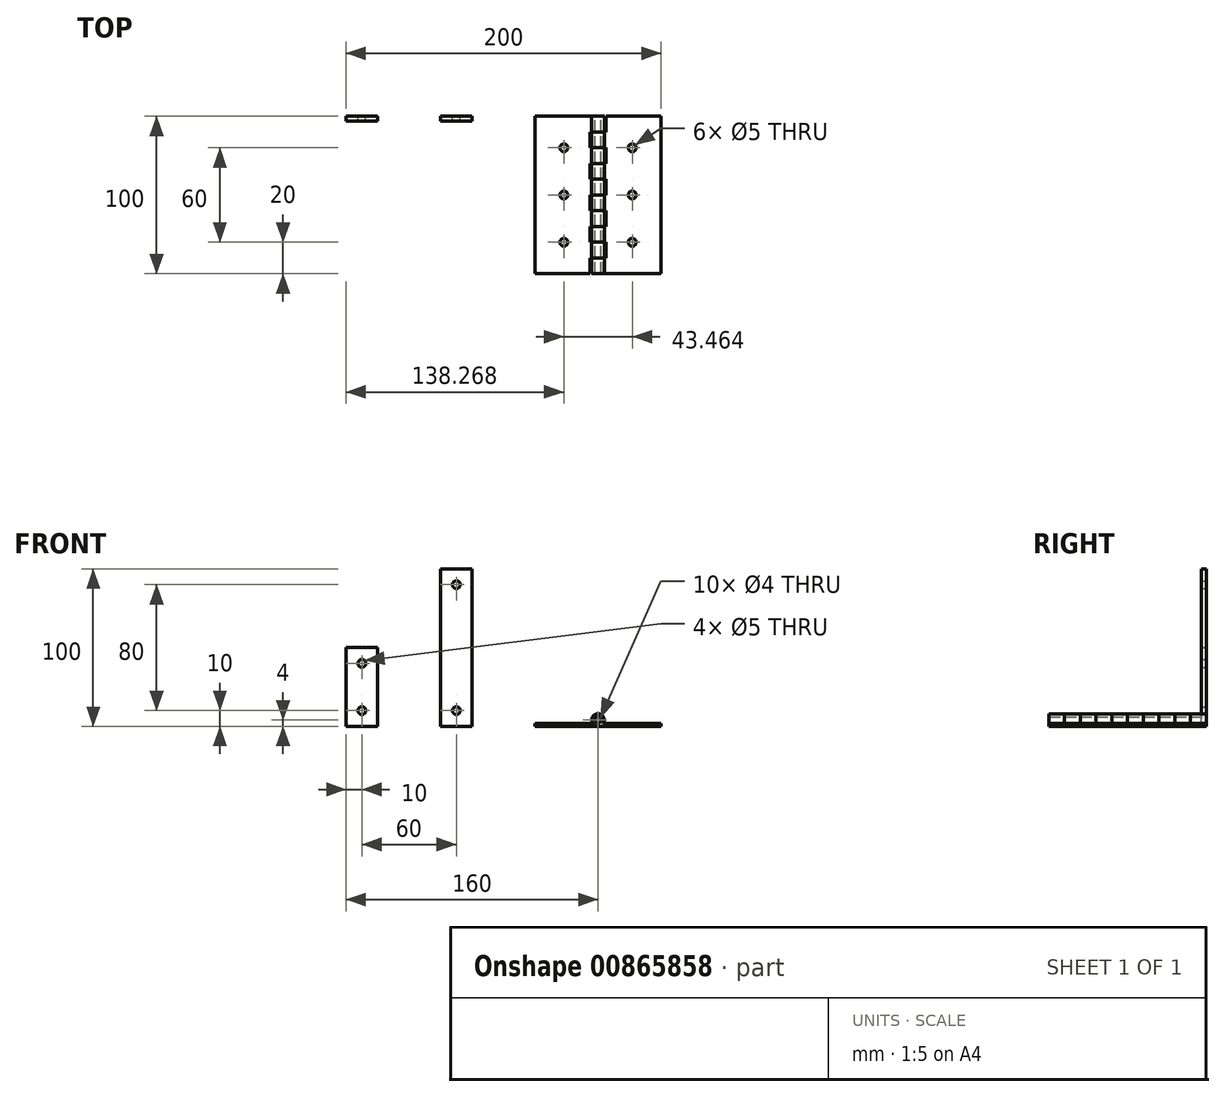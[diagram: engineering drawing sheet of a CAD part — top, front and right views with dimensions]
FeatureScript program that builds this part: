
annotation { "Feature Type Name" : "Feature", "Feature Type Description" : "" }
export const myFeature = defineFeature(function(context is Context, id is Id, definition is map)
    precondition{}
    {
        {
            var Q0;
            Q0=qCreatedBy(makeId("Front.planeOp"),FACE);
            var sketch = newSketch(context, id + "F0", { "sketchPlane" : qUnion([Q0])});
            skLineSegment(sketch, "E0.bottom", {"start": v(-50, 60) * mm, "end": v(-30, 60) * mm});
            skLineSegment(sketch, "E0.top", {"start": v(-50, 10) * mm, "end": v(-30, 10) * mm});
            skLineSegment(sketch, "E0.left", {"start": v(-50, 60) * mm, "end": v(-50, 10) * mm});
            skLineSegment(sketch, "E0.right", {"start": v(-30, 60) * mm, "end": v(-30, 10) * mm});
            skLineSegment(sketch, "E1.bottom", {"start": v(10, 10) * mm, "end": v(30, 10) * mm});
            skLineSegment(sketch, "E1.top", {"start": v(10, 110) * mm, "end": v(30, 110) * mm});
            skLineSegment(sketch, "E1.left", {"start": v(10, 10) * mm, "end": v(10, 110) * mm});
            skLineSegment(sketch, "E1.right", {"start": v(30, 10) * mm, "end": v(30, 110) * mm});
            skLineSegment(sketch, "E2", {"start": v(-40, 10) * mm, "end": v(-40, 60) * mm, "construction": true});
            skCircle(sketch, "E3", {"center": v(-40, 50) * mm, "radius": 2.5 * mm});
            skCircle(sketch, "E4", {"center": v(-40, 20) * mm, "radius": 2.5 * mm});
            skLineSegment(sketch, "E5", {"start": v(20, 10) * mm, "end": v(20, 110) * mm, "construction": true});
            skCircle(sketch, "E6", {"center": v(20, 100) * mm, "radius": 2.5 * mm});
            skCircle(sketch, "E7", {"center": v(20, 20) * mm, "radius": 2.5 * mm});
            skLineSegment(sketch, "E8.bottom", {"start": v(70, 10) * mm, "end": v(110, 10) * mm});
            skLineSegment(sketch, "E8.top", {"start": v(70, 12) * mm, "end": v(110, 12) * mm});
            skLineSegment(sketch, "E8.left", {"start": v(70, 10) * mm, "end": v(70, 12) * mm});
            skLineSegment(sketch, "E8.right", {"start": v(110, 10) * mm, "end": v(110, 12) * mm});
            skCircle(sketch, "E9", {"center": v(110, 14) * mm, "radius": 4 * mm});
            skCircle(sketch, "E10", {"center": v(110, 14) * mm, "radius": 2 * mm});
            skSolve(sketch);
        }
        {
            var Q0;
            Q0=makeQuery(id+"F0.imprint","IMPRINT",FACE,{"disambiguationData":[TD([[makeQuery(id+"F0.imprint","IMPRINT",EDGE,{"derivedFrom":sQuery(id+"F0.wireOp",EDGE,"E0.bottom")}),-1.0]])]});
            var Q1;
            Q1=makeQuery(id+"F0.imprint","IMPRINT",FACE,{"disambiguationData":[TD([[makeQuery(id+"F0.imprint","IMPRINT",EDGE,{"derivedFrom":sQuery(id+"F0.wireOp",EDGE,"E1.bottom")}),1.0]])]});
            var Q2;
            {var subQ0=sQuery(id+"F0.wireOp",EDGE,"E8.bottom");Q2=makeQuery(id+"F0.imprint","IMPRINT",FACE,{"disambiguationData":[TD([[makeQuery(id+"F0.imprint","IMPRINT",EDGE,{"derivedFrom":subQ0}),1.0]])]});}
            var Q3;
            {var subQ0=sQuery(id+"F0.wireOp",EDGE,"E8.right");Q3=makeQuery(id+"F0.imprint","IMPRINT",FACE,{"disambiguationData":[TD([[makeQuery(id+"F0.imprint","IMPRINT",EDGE,{"derivedFrom":subQ0}),1.0]])]});}
            var Q4;
            {var subQ1=sQuery(id+"F0.wireOp",EDGE,"E8.right");Q4=makeQuery(id+"F0.imprint","IMPRINT",FACE,{"disambiguationData":[TD([[makeQuery(id+"F0.imprint","IMPRINT",EDGE,{"derivedFrom":subQ1}),-1.0]])]});}
            extrude(context, id + "F1", {"entities" : qUnion([Q0, Q1, Q2, Q3, Q4]), "depth" : 3 * mm, "offsetDistance" : 25 * mm});
        }
        {
            var Q0;
            Q0=makeQuery(id+"F1.opExtrude","CAP_FACE",FACE,{"disambiguationData":[OSD([sQuery(id+"F0.wireOp",EDGE,"E8.bottom"),sQuery(id+"F0.wireOp",EDGE,"E8.top"),sQuery(id+"F0.wireOp",EDGE,"E8.left"),sQuery(id+"F0.wireOp",EDGE,"E9"),sQuery(id+"F0.wireOp",EDGE,"E10")])],"isStart":false});
            extrude(context, id + "F2", {"entities" : qUnion([Q0]), "operationType" : NewBodyOperationType.ADD, "depth" : 97 * mm, "offsetDistance" : 25 * mm});
        }
        {
            var Q0;
            Q0=makeQuery(id+"F2.opExtrude","CAP_VERTEX",VERTEX,{"disambiguationData":[OSD([sQuery(id+"F0.wireOp",EDGE,"E8.bottom"),sQuery(id+"F0.wireOp",EDGE,"E8.right"),sQuery(id+"F0.wireOp",EDGE,"E9")])],"isStart":false});
            var Q1;
            Q1=makeQuery(id+"F2.opExtrude","CAP_EDGE",EDGE,{"disambiguationData":[OSD([sQuery(id+"F0.wireOp",EDGE,"E8.bottom")])],"isStart":false});
            cPlane(context, id + "F3", {"entities" : qUnion([Q0, Q1]), "cplaneType" : CPlaneType.LINE_POINT, "offset" : 25 * mm, "width" : 150 * mm, "height" : 150 * mm});
        }
        {
            var Q0;
            {var subQ0=sQuery(id+"F0.wireOp",EDGE,"E8.top");Q0=makeQuery(id+"F2.boolean.opBoolean","MERGE",FACE,{"derivedFrom":[makeQuery(id+"F1.opExtrude","SWEPT_FACE",FACE,{"disambiguationData":[OSD([subQ0])]}),makeQuery(id+"F2.opExtrude","SWEPT_FACE",FACE,{"disambiguationData":[OSD([subQ0])]})]});}
            var sketch = newSketch(context, id + "F4", { "sketchPlane" : qUnion([Q0])});
            skLineSegment(sketch, "E11", {"start": v(88.27, -100) * mm, "end": v(88.27, 0) * mm, "construction": true});
            skCircle(sketch, "E12", {"center": v(88.27, -80) * mm, "radius": 2.5 * mm});
            skCircle(sketch, "E13", {"center": v(88.27, -50) * mm, "radius": 2.5 * mm});
            skCircle(sketch, "E14", {"center": v(88.27, -20) * mm, "radius": 2.5 * mm});
            skSolve(sketch);
        }
        {
            var Q0;
            Q0=makeQuery(id+"F4.imprint","IMPRINT",FACE,{"disambiguationData":[TD([[makeQuery(id+"F4.imprint","IMPRINT",EDGE,{"derivedFrom":sQuery(id+"F4.wireOp",EDGE,"E12")}),1.0]])]});
            var Q1;
            Q1=makeQuery(id+"F4.imprint","IMPRINT",FACE,{"disambiguationData":[TD([[makeQuery(id+"F4.imprint","IMPRINT",EDGE,{"derivedFrom":sQuery(id+"F4.wireOp",EDGE,"E13")}),1.0]])]});
            var Q2;
            Q2=makeQuery(id+"F4.imprint","IMPRINT",FACE,{"disambiguationData":[TD([[makeQuery(id+"F4.imprint","IMPRINT",EDGE,{"derivedFrom":sQuery(id+"F4.wireOp",EDGE,"E14")}),1.0]])]});
            extrude(context, id + "F5", {"entities" : qUnion([Q0, Q1, Q2]), "operationType" : NewBodyOperationType.REMOVE, "endBound" : BoundingType.THROUGH_ALL, "oppositeDirection" : true, "depth" : 25 * mm, "offsetDistance" : 25 * mm});
        }
        {
            var Q0;
            Q0=makeQuery(id+"F1.opExtrude","SWEPT_BODY",BODY,{"disambiguationData":[OSD([sQuery(id+"F0.wireOp",EDGE,"E8.bottom"),sQuery(id+"F0.wireOp",EDGE,"E8.top"),sQuery(id+"F0.wireOp",EDGE,"E8.left"),sQuery(id+"F0.wireOp",EDGE,"E9"),sQuery(id+"F0.wireOp",EDGE,"E10")])]});
            var Q1;
            Q1=qCreatedBy(id+"F3.planeOp",FACE);
            mirror(context, id + "F6", {"entities" : qUnion([Q0]), "mirrorPlane" : qUnion([Q1])});
        }
        {
            var Q0;
            {var subQ0=sQuery(id+"F0.wireOp",EDGE,"E8.top");Q0=makeQuery(id+"F6.opPattern","COPY",FACE,{"derivedFrom":makeQuery(id+"F2.boolean.opBoolean","MERGE",FACE,{"derivedFrom":[makeQuery(id+"F1.opExtrude","SWEPT_FACE",FACE,{"disambiguationData":[OSD([subQ0])]}),makeQuery(id+"F2.opExtrude","SWEPT_FACE",FACE,{"disambiguationData":[OSD([subQ0])]})]}),"instanceName":"1"});}
            var sketch = newSketch(context, id + "F7", { "sketchPlane" : qUnion([Q0])});
            skLineSegment(sketch, "E15.bottom", {"start": v(150, -90) * mm, "end": v(140, -90) * mm});
            skLineSegment(sketch, "E15.top", {"start": v(150, -80) * mm, "end": v(140, -80) * mm});
            skLineSegment(sketch, "E15.left", {"start": v(150, -90) * mm, "end": v(150, -80) * mm});
            skLineSegment(sketch, "E15.right", {"start": v(140, -90) * mm, "end": v(140, -80) * mm});
            skSolve(sketch);
        }
        {
            var Q0;
            Q0=makeQuery(id+"F7.imprint","IMPRINT",FACE,{"disambiguationData":[TD([[makeQuery(id+"F7.imprint","IMPRINT",EDGE,{"derivedFrom":sQuery(id+"F7.wireOp",EDGE,"E15.bottom")}),-1.0]])]});
            extrude(context, id + "F8", {"entities" : qUnion([Q0]), "depth" : 10 * mm, "offsetDistance" : 25 * mm});
        }
        {
            var Q0;
            Q0=makeQuery(id+"F8.opExtrude","SWEPT_BODY",BODY,{"disambiguationData":[OSD([sQuery(id+"F7.wireOp",EDGE,"E15.bottom"),sQuery(id+"F7.wireOp",EDGE,"E15.top"),sQuery(id+"F7.wireOp",EDGE,"E15.left"),sQuery(id+"F7.wireOp",EDGE,"E15.right")])]});
            var Q1;
            Q1=makeQuery(id+"F6.opPattern","COPY",EDGE,{"derivedFrom":makeQuery(id+"F2.opExtrude","CAP_EDGE",EDGE,{"disambiguationData":[OSD([sQuery(id+"F0.wireOp",EDGE,"E8.left")])],"isStart":false}),"instanceName":"1"});
            transform(context, id + "F9", {"entities" : qUnion([Q0]), "transformType" : TransformType.TRANSLATION_ENTITY, "oppositeDirectionEntity" : true, "transformLine" : qUnion([Q1]), "makeCopy" : false});
        }
        {
            var Q0;
            Q0=makeQuery(id+"F8.opExtrude","SWEPT_BODY",BODY,{"disambiguationData":[OSD([sQuery(id+"F7.wireOp",EDGE,"E15.bottom"),sQuery(id+"F7.wireOp",EDGE,"E15.top"),sQuery(id+"F7.wireOp",EDGE,"E15.left"),sQuery(id+"F7.wireOp",EDGE,"E15.right")])]});
            var Q1;
            {var subQ0=sQuery(id+"F0.wireOp",EDGE,"E8.left");var subQ1=sQuery(id+"F0.wireOp",EDGE,"E8.top");Q1=makeQuery(id+"F6.opPattern","COPY",EDGE,{"derivedFrom":makeQuery(id+"F2.boolean.opBoolean","MERGE",EDGE,{"derivedFrom":[makeQuery(id+"F1.opExtrude","SWEPT_EDGE",EDGE,{"disambiguationData":[OSD([subQ1,subQ0])]}),makeQuery(id+"F2.opExtrude","SWEPT_EDGE",EDGE,{"disambiguationData":[OSD([subQ1,subQ0])]})]}),"instanceName":"1"});}
            transform(context, id + "F10", {"entities" : qUnion([Q0]), "transformType" : TransformType.TRANSLATION_DISTANCE, "transformDirection" : qUnion([Q1]), "distance" : 20 * mm, "makeCopy" : true});
        }
        {
            var Q0;
            Q0=makeQuery(id+"F8.opExtrude","SWEPT_BODY",BODY,{"disambiguationData":[OSD([sQuery(id+"F7.wireOp",EDGE,"E15.bottom"),sQuery(id+"F7.wireOp",EDGE,"E15.top"),sQuery(id+"F7.wireOp",EDGE,"E15.left"),sQuery(id+"F7.wireOp",EDGE,"E15.right")])]});
            var Q1;
            Q1=makeQuery(id+"F10.opPattern","COPY",BODY,{"derivedFrom":makeQuery(id+"F8.opExtrude","SWEPT_BODY",BODY,{"disambiguationData":[OSD([sQuery(id+"F7.wireOp",EDGE,"E15.bottom"),sQuery(id+"F7.wireOp",EDGE,"E15.top"),sQuery(id+"F7.wireOp",EDGE,"E15.left"),sQuery(id+"F7.wireOp",EDGE,"E15.right")])]}),"instanceName":"1"});
            var Q2;
            {var subQ0=sQuery(id+"F0.wireOp",EDGE,"E8.left");var subQ1=sQuery(id+"F0.wireOp",EDGE,"E8.top");Q2=makeQuery(id+"F6.opPattern","COPY",EDGE,{"derivedFrom":makeQuery(id+"F2.boolean.opBoolean","MERGE",EDGE,{"derivedFrom":[makeQuery(id+"F1.opExtrude","SWEPT_EDGE",EDGE,{"disambiguationData":[OSD([subQ1,subQ0])]}),makeQuery(id+"F2.opExtrude","SWEPT_EDGE",EDGE,{"disambiguationData":[OSD([subQ1,subQ0])]})]}),"instanceName":"1"});}
            transform(context, id + "F11", {"entities" : qUnion([Q0, Q1]), "transformType" : TransformType.TRANSLATION_DISTANCE, "transformDirection" : qUnion([Q2]), "distance" : 40 * mm, "makeCopy" : true});
        }
        {
            var Q0;
            Q0=makeQuery(id+"F11.opPattern","COPY",BODY,{"derivedFrom":makeQuery(id+"F10.opPattern","COPY",BODY,{"derivedFrom":makeQuery(id+"F8.opExtrude","SWEPT_BODY",BODY,{"disambiguationData":[OSD([sQuery(id+"F7.wireOp",EDGE,"E15.bottom"),sQuery(id+"F7.wireOp",EDGE,"E15.top"),sQuery(id+"F7.wireOp",EDGE,"E15.left"),sQuery(id+"F7.wireOp",EDGE,"E15.right")])]}),"instanceName":"1"}),"instanceName":"1"});
            var Q1;
            {var subQ0=sQuery(id+"F0.wireOp",EDGE,"E8.left");var subQ1=sQuery(id+"F0.wireOp",EDGE,"E8.top");Q1=makeQuery(id+"F6.opPattern","COPY",EDGE,{"derivedFrom":makeQuery(id+"F2.boolean.opBoolean","MERGE",EDGE,{"derivedFrom":[makeQuery(id+"F1.opExtrude","SWEPT_EDGE",EDGE,{"disambiguationData":[OSD([subQ1,subQ0])]}),makeQuery(id+"F2.opExtrude","SWEPT_EDGE",EDGE,{"disambiguationData":[OSD([subQ1,subQ0])]})]}),"instanceName":"1"});}
            transform(context, id + "F12", {"entities" : qUnion([Q0]), "transformType" : TransformType.TRANSLATION_DISTANCE, "transformDirection" : qUnion([Q1]), "distance" : 20 * mm, "makeCopy" : true});
        }
        {
            var Q0;
            Q0=makeQuery(id+"F8.opExtrude","SWEPT_BODY",BODY,{"disambiguationData":[OSD([sQuery(id+"F7.wireOp",EDGE,"E15.bottom"),sQuery(id+"F7.wireOp",EDGE,"E15.top"),sQuery(id+"F7.wireOp",EDGE,"E15.left"),sQuery(id+"F7.wireOp",EDGE,"E15.right")])]});
            var Q1;
            Q1=makeQuery(id+"F10.opPattern","COPY",BODY,{"derivedFrom":makeQuery(id+"F8.opExtrude","SWEPT_BODY",BODY,{"disambiguationData":[OSD([sQuery(id+"F7.wireOp",EDGE,"E15.bottom"),sQuery(id+"F7.wireOp",EDGE,"E15.top"),sQuery(id+"F7.wireOp",EDGE,"E15.left"),sQuery(id+"F7.wireOp",EDGE,"E15.right")])]}),"instanceName":"1"});
            var Q2;
            Q2=makeQuery(id+"F11.opPattern","COPY",BODY,{"derivedFrom":makeQuery(id+"F8.opExtrude","SWEPT_BODY",BODY,{"disambiguationData":[OSD([sQuery(id+"F7.wireOp",EDGE,"E15.bottom"),sQuery(id+"F7.wireOp",EDGE,"E15.top"),sQuery(id+"F7.wireOp",EDGE,"E15.left"),sQuery(id+"F7.wireOp",EDGE,"E15.right")])]}),"instanceName":"1"});
            var Q3;
            Q3=makeQuery(id+"F11.opPattern","COPY",BODY,{"derivedFrom":makeQuery(id+"F10.opPattern","COPY",BODY,{"derivedFrom":makeQuery(id+"F8.opExtrude","SWEPT_BODY",BODY,{"disambiguationData":[OSD([sQuery(id+"F7.wireOp",EDGE,"E15.bottom"),sQuery(id+"F7.wireOp",EDGE,"E15.top"),sQuery(id+"F7.wireOp",EDGE,"E15.left"),sQuery(id+"F7.wireOp",EDGE,"E15.right")])]}),"instanceName":"1"}),"instanceName":"1"});
            var Q4;
            Q4=makeQuery(id+"F12.opPattern","COPY",BODY,{"derivedFrom":makeQuery(id+"F11.opPattern","COPY",BODY,{"derivedFrom":makeQuery(id+"F10.opPattern","COPY",BODY,{"derivedFrom":makeQuery(id+"F8.opExtrude","SWEPT_BODY",BODY,{"disambiguationData":[OSD([sQuery(id+"F7.wireOp",EDGE,"E15.bottom"),sQuery(id+"F7.wireOp",EDGE,"E15.top"),sQuery(id+"F7.wireOp",EDGE,"E15.left"),sQuery(id+"F7.wireOp",EDGE,"E15.right")])]}),"instanceName":"1"}),"instanceName":"1"}),"instanceName":"1"});
            var Q5;
            Q5=makeQuery(id+"F6.opPattern","COPY",EDGE,{"derivedFrom":makeQuery(id+"F2.opExtrude","CAP_EDGE",EDGE,{"disambiguationData":[OSD([sQuery(id+"F0.wireOp",EDGE,"E8.bottom")])],"isStart":false}),"instanceName":"1"});
            transform(context, id + "F13", {"entities" : qUnion([Q0, Q1, Q2, Q3, Q4]), "transformType" : TransformType.TRANSLATION_ENTITY, "oppositeDirectionEntity" : false, "transformLine" : qUnion([Q5]), "makeCopy" : false});
        }
        {
            var Q0;
            Q0=makeQuery(id+"F12.opPattern","COPY",BODY,{"derivedFrom":makeQuery(id+"F11.opPattern","COPY",BODY,{"derivedFrom":makeQuery(id+"F10.opPattern","COPY",BODY,{"derivedFrom":makeQuery(id+"F8.opExtrude","SWEPT_BODY",BODY,{"disambiguationData":[OSD([sQuery(id+"F7.wireOp",EDGE,"E15.bottom"),sQuery(id+"F7.wireOp",EDGE,"E15.top"),sQuery(id+"F7.wireOp",EDGE,"E15.left"),sQuery(id+"F7.wireOp",EDGE,"E15.right")])]}),"instanceName":"1"}),"instanceName":"1"}),"instanceName":"1"});
            var Q1;
            Q1=makeQuery(id+"F11.opPattern","COPY",BODY,{"derivedFrom":makeQuery(id+"F10.opPattern","COPY",BODY,{"derivedFrom":makeQuery(id+"F8.opExtrude","SWEPT_BODY",BODY,{"disambiguationData":[OSD([sQuery(id+"F7.wireOp",EDGE,"E15.bottom"),sQuery(id+"F7.wireOp",EDGE,"E15.top"),sQuery(id+"F7.wireOp",EDGE,"E15.left"),sQuery(id+"F7.wireOp",EDGE,"E15.right")])]}),"instanceName":"1"}),"instanceName":"1"});
            var Q2;
            Q2=makeQuery(id+"F11.opPattern","COPY",BODY,{"derivedFrom":makeQuery(id+"F8.opExtrude","SWEPT_BODY",BODY,{"disambiguationData":[OSD([sQuery(id+"F7.wireOp",EDGE,"E15.bottom"),sQuery(id+"F7.wireOp",EDGE,"E15.top"),sQuery(id+"F7.wireOp",EDGE,"E15.left"),sQuery(id+"F7.wireOp",EDGE,"E15.right")])]}),"instanceName":"1"});
            var Q3;
            Q3=makeQuery(id+"F10.opPattern","COPY",BODY,{"derivedFrom":makeQuery(id+"F8.opExtrude","SWEPT_BODY",BODY,{"disambiguationData":[OSD([sQuery(id+"F7.wireOp",EDGE,"E15.bottom"),sQuery(id+"F7.wireOp",EDGE,"E15.top"),sQuery(id+"F7.wireOp",EDGE,"E15.left"),sQuery(id+"F7.wireOp",EDGE,"E15.right")])]}),"instanceName":"1"});
            var Q4;
            Q4=makeQuery(id+"F8.opExtrude","SWEPT_BODY",BODY,{"disambiguationData":[OSD([sQuery(id+"F7.wireOp",EDGE,"E15.bottom"),sQuery(id+"F7.wireOp",EDGE,"E15.top"),sQuery(id+"F7.wireOp",EDGE,"E15.left"),sQuery(id+"F7.wireOp",EDGE,"E15.right")])]});
            var Q5;
            Q5=makeQuery(id+"F6.opPattern","COPY",EDGE,{"derivedFrom":makeQuery(id+"F2.opExtrude","CAP_EDGE",EDGE,{"disambiguationData":[OSD([sQuery(id+"F0.wireOp",EDGE,"E8.top")])],"isStart":false}),"instanceName":"1"});
            var Q6;
            Q6=makeQuery(id+"F6.opPattern","COPY",EDGE,{"derivedFrom":makeQuery(id+"F2.opExtrude","CAP_EDGE",EDGE,{"disambiguationData":[OSD([sQuery(id+"F0.wireOp",EDGE,"E8.top")])],"isStart":false}),"instanceName":"1"});
            transform(context, id + "F14", {"entities" : qUnion([Q0, Q1, Q2, Q3, Q4]), "transformType" : TransformType.TRANSLATION_DISTANCE, "transformDirection" : qUnion([Q6]), "distance" : 5 * mm, "oppositeDirection" : true, "makeCopy" : false});
        }
        {
            var Q0;
            Q0=makeQuery(id+"F1.opExtrude","SWEPT_BODY",BODY,{"disambiguationData":[OSD([sQuery(id+"F0.wireOp",EDGE,"E8.bottom"),sQuery(id+"F0.wireOp",EDGE,"E8.top"),sQuery(id+"F0.wireOp",EDGE,"E8.left"),sQuery(id+"F0.wireOp",EDGE,"E9"),sQuery(id+"F0.wireOp",EDGE,"E10")])]});
            var Q1;
            {var subQ0=sQuery(id+"F0.wireOp",EDGE,"E8.left");var subQ1=sQuery(id+"F0.wireOp",EDGE,"E8.top");Q1=makeQuery(id+"F2.boolean.opBoolean","MERGE",EDGE,{"derivedFrom":[makeQuery(id+"F1.opExtrude","SWEPT_EDGE",EDGE,{"disambiguationData":[OSD([subQ1,subQ0])]}),makeQuery(id+"F2.opExtrude","SWEPT_EDGE",EDGE,{"disambiguationData":[OSD([subQ1,subQ0])]})]});}
            transform(context, id + "F15", {"entities" : qUnion([Q0]), "transformType" : TransformType.TRANSLATION_DISTANCE, "transformDirection" : qUnion([Q1]), "distance" : 10 * mm, "makeCopy" : false});
        }
        {
            var Q0;
            Q0=makeQuery(id+"F12.opPattern","COPY",BODY,{"derivedFrom":makeQuery(id+"F11.opPattern","COPY",BODY,{"derivedFrom":makeQuery(id+"F10.opPattern","COPY",BODY,{"derivedFrom":makeQuery(id+"F8.opExtrude","SWEPT_BODY",BODY,{"disambiguationData":[OSD([sQuery(id+"F7.wireOp",EDGE,"E15.bottom"),sQuery(id+"F7.wireOp",EDGE,"E15.top"),sQuery(id+"F7.wireOp",EDGE,"E15.left"),sQuery(id+"F7.wireOp",EDGE,"E15.right")])]}),"instanceName":"1"}),"instanceName":"1"}),"instanceName":"1"});
            var Q1;
            Q1=makeQuery(id+"F11.opPattern","COPY",BODY,{"derivedFrom":makeQuery(id+"F10.opPattern","COPY",BODY,{"derivedFrom":makeQuery(id+"F8.opExtrude","SWEPT_BODY",BODY,{"disambiguationData":[OSD([sQuery(id+"F7.wireOp",EDGE,"E15.bottom"),sQuery(id+"F7.wireOp",EDGE,"E15.top"),sQuery(id+"F7.wireOp",EDGE,"E15.left"),sQuery(id+"F7.wireOp",EDGE,"E15.right")])]}),"instanceName":"1"}),"instanceName":"1"});
            var Q2;
            Q2=makeQuery(id+"F11.opPattern","COPY",BODY,{"derivedFrom":makeQuery(id+"F8.opExtrude","SWEPT_BODY",BODY,{"disambiguationData":[OSD([sQuery(id+"F7.wireOp",EDGE,"E15.bottom"),sQuery(id+"F7.wireOp",EDGE,"E15.top"),sQuery(id+"F7.wireOp",EDGE,"E15.left"),sQuery(id+"F7.wireOp",EDGE,"E15.right")])]}),"instanceName":"1"});
            var Q3;
            Q3=makeQuery(id+"F10.opPattern","COPY",BODY,{"derivedFrom":makeQuery(id+"F8.opExtrude","SWEPT_BODY",BODY,{"disambiguationData":[OSD([sQuery(id+"F7.wireOp",EDGE,"E15.bottom"),sQuery(id+"F7.wireOp",EDGE,"E15.top"),sQuery(id+"F7.wireOp",EDGE,"E15.left"),sQuery(id+"F7.wireOp",EDGE,"E15.right")])]}),"instanceName":"1"});
            var Q4;
            Q4=makeQuery(id+"F8.opExtrude","SWEPT_BODY",BODY,{"disambiguationData":[OSD([sQuery(id+"F7.wireOp",EDGE,"E15.bottom"),sQuery(id+"F7.wireOp",EDGE,"E15.top"),sQuery(id+"F7.wireOp",EDGE,"E15.left"),sQuery(id+"F7.wireOp",EDGE,"E15.right")])]});
            var Q5;
            Q5=makeQuery(id+"F1.opExtrude","SWEPT_BODY",BODY,{"disambiguationData":[OSD([sQuery(id+"F0.wireOp",EDGE,"E8.bottom"),sQuery(id+"F0.wireOp",EDGE,"E8.top"),sQuery(id+"F0.wireOp",EDGE,"E8.left"),sQuery(id+"F0.wireOp",EDGE,"E9"),sQuery(id+"F0.wireOp",EDGE,"E10")])]});
            booleanBodies(context, id + "F16", {"operationType" : BooleanOperationType.SUBTRACTION, "tools" : qUnion([Q0, Q1, Q2, Q3, Q4]), "targets" : qUnion([Q5]), "keepTools" : true});
        }
        {
            var Q0;
            Q0=makeQuery(id+"F12.opPattern","COPY",BODY,{"derivedFrom":makeQuery(id+"F11.opPattern","COPY",BODY,{"derivedFrom":makeQuery(id+"F10.opPattern","COPY",BODY,{"derivedFrom":makeQuery(id+"F8.opExtrude","SWEPT_BODY",BODY,{"disambiguationData":[OSD([sQuery(id+"F7.wireOp",EDGE,"E15.bottom"),sQuery(id+"F7.wireOp",EDGE,"E15.top"),sQuery(id+"F7.wireOp",EDGE,"E15.left"),sQuery(id+"F7.wireOp",EDGE,"E15.right")])]}),"instanceName":"1"}),"instanceName":"1"}),"instanceName":"1"});
            var Q1;
            Q1=makeQuery(id+"F11.opPattern","COPY",BODY,{"derivedFrom":makeQuery(id+"F10.opPattern","COPY",BODY,{"derivedFrom":makeQuery(id+"F8.opExtrude","SWEPT_BODY",BODY,{"disambiguationData":[OSD([sQuery(id+"F7.wireOp",EDGE,"E15.bottom"),sQuery(id+"F7.wireOp",EDGE,"E15.top"),sQuery(id+"F7.wireOp",EDGE,"E15.left"),sQuery(id+"F7.wireOp",EDGE,"E15.right")])]}),"instanceName":"1"}),"instanceName":"1"});
            var Q2;
            Q2=makeQuery(id+"F11.opPattern","COPY",BODY,{"derivedFrom":makeQuery(id+"F8.opExtrude","SWEPT_BODY",BODY,{"disambiguationData":[OSD([sQuery(id+"F7.wireOp",EDGE,"E15.bottom"),sQuery(id+"F7.wireOp",EDGE,"E15.top"),sQuery(id+"F7.wireOp",EDGE,"E15.left"),sQuery(id+"F7.wireOp",EDGE,"E15.right")])]}),"instanceName":"1"});
            var Q3;
            Q3=makeQuery(id+"F10.opPattern","COPY",BODY,{"derivedFrom":makeQuery(id+"F8.opExtrude","SWEPT_BODY",BODY,{"disambiguationData":[OSD([sQuery(id+"F7.wireOp",EDGE,"E15.bottom"),sQuery(id+"F7.wireOp",EDGE,"E15.top"),sQuery(id+"F7.wireOp",EDGE,"E15.left"),sQuery(id+"F7.wireOp",EDGE,"E15.right")])]}),"instanceName":"1"});
            var Q4;
            Q4=makeQuery(id+"F8.opExtrude","SWEPT_BODY",BODY,{"disambiguationData":[OSD([sQuery(id+"F7.wireOp",EDGE,"E15.bottom"),sQuery(id+"F7.wireOp",EDGE,"E15.top"),sQuery(id+"F7.wireOp",EDGE,"E15.left"),sQuery(id+"F7.wireOp",EDGE,"E15.right")])]});
            var Q5;
            Q5=makeQuery(id+"F6.opPattern","COPY",BODY,{"derivedFrom":makeQuery(id+"F1.opExtrude","SWEPT_BODY",BODY,{"disambiguationData":[OSD([sQuery(id+"F0.wireOp",EDGE,"E8.bottom"),sQuery(id+"F0.wireOp",EDGE,"E8.top"),sQuery(id+"F0.wireOp",EDGE,"E8.left"),sQuery(id+"F0.wireOp",EDGE,"E9"),sQuery(id+"F0.wireOp",EDGE,"E10")])]}),"instanceName":"1"});
            booleanBodies(context, id + "F17", {"operationType" : BooleanOperationType.SUBTRACTION, "tools" : qUnion([Q0, Q1, Q2, Q3, Q4]), "targets" : qUnion([Q5])});
        }
        {
            var Q0;
            Q0=makeQuery(id+"F1.opExtrude","SWEPT_BODY",BODY,{"disambiguationData":[OSD([sQuery(id+"F0.wireOp",EDGE,"E8.bottom"),sQuery(id+"F0.wireOp",EDGE,"E8.top"),sQuery(id+"F0.wireOp",EDGE,"E8.left"),sQuery(id+"F0.wireOp",EDGE,"E9"),sQuery(id+"F0.wireOp",EDGE,"E10")])]});
            var Q1;
            {var subQ0=sQuery(id+"F0.wireOp",EDGE,"E8.top");Q1=makeQuery(id+"F16.opBoolean","INTERSECT",EDGE,{"derivedFrom":[makeQuery(id+"F12.opPattern","COPY",FACE,{"derivedFrom":makeQuery(id+"F11.opPattern","COPY",FACE,{"derivedFrom":makeQuery(id+"F10.opPattern","COPY",FACE,{"derivedFrom":makeQuery(id+"F8.opExtrude","SWEPT_FACE",FACE,{"disambiguationData":[OSD([sQuery(id+"F7.wireOp",EDGE,"E15.right")])]}),"instanceName":"1"}),"instanceName":"1"}),"instanceName":"1"}),makeQuery(id+"F2.boolean.opBoolean","MERGE",FACE,{"derivedFrom":[makeQuery(id+"F1.opExtrude","SWEPT_FACE",FACE,{"disambiguationData":[OSD([subQ0])]}),makeQuery(id+"F2.opExtrude","SWEPT_FACE",FACE,{"disambiguationData":[OSD([subQ0])]})]})]});}
            transform(context, id + "F18", {"entities" : qUnion([Q0]), "transformType" : TransformType.TRANSLATION_ENTITY, "oppositeDirectionEntity" : false, "transformLine" : qUnion([Q1]), "makeCopy" : false});
        }
    });
